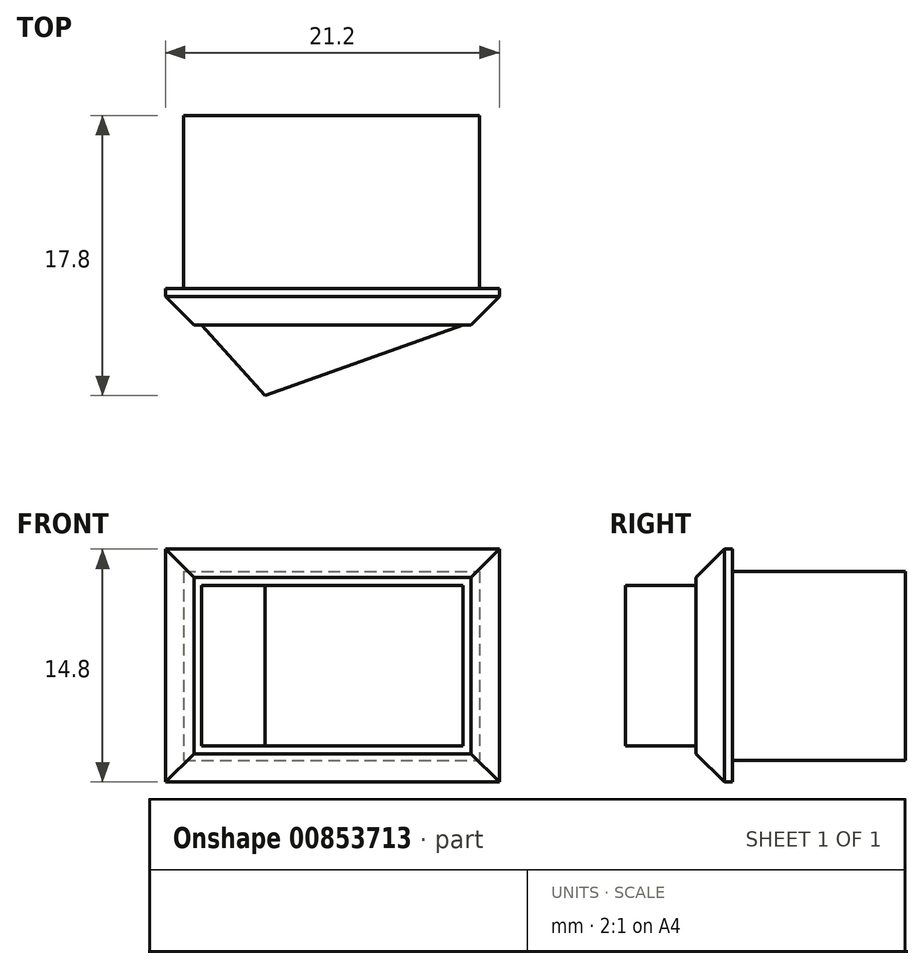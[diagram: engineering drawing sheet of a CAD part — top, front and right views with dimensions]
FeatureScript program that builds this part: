
annotation { "Feature Type Name" : "Feature", "Feature Type Description" : "" }
export const myFeature = defineFeature(function(context is Context, id is Id, definition is map)
    precondition{}
    {
        {
            var Q0;
            Q0=qCreatedBy(makeId("Front.planeOp"),FACE);
            var sketch = newSketch(context, id + "F0", { "sketchPlane" : qUnion([Q0])});
            skLineSegment(sketch, "E0.bottom", {"start": v(0, 0) * mm, "end": v(18.8, 0) * mm});
            skLineSegment(sketch, "E0.top", {"start": v(0, -12) * mm, "end": v(18.8, -12) * mm});
            skLineSegment(sketch, "E0.left", {"start": v(0, 0) * mm, "end": v(0, -12) * mm});
            skLineSegment(sketch, "E0.right", {"start": v(18.8, 0) * mm, "end": v(18.8, -12) * mm});
            skSolve(sketch);
        }
        {
            var Q0;
            Q0 = qSketchRegion(id + "F0", true);
            extrude(context, id + "F1", {"entities" : qUnion([Q0]), "depth" : 11 * mm, "offsetDistance" : 25 * mm});
        }
        {
            var Q0;
            Q0=makeQuery(id+"F1.opExtrude","CAP_FACE",FACE,{"disambiguationData":[OSD([sQuery(id+"F0.wireOp",EDGE,"E0.bottom"),sQuery(id+"F0.wireOp",EDGE,"E0.top"),sQuery(id+"F0.wireOp",EDGE,"E0.left"),sQuery(id+"F0.wireOp",EDGE,"E0.right")])],"isStart":false});
            var sketch = newSketch(context, id + "F2", { "sketchPlane" : qUnion([Q0])});
            skLineSegment(sketch, "E1.bottom", {"start": v(-1.15, 1.4) * mm, "end": v(20.05, 1.4) * mm});
            skLineSegment(sketch, "E1.top", {"start": v(-1.15, -13.4) * mm, "end": v(20.05, -13.4) * mm});
            skLineSegment(sketch, "E1.left", {"start": v(-1.15, 1.4) * mm, "end": v(-1.15, -13.4) * mm});
            skLineSegment(sketch, "E1.right", {"start": v(20.05, 1.4) * mm, "end": v(20.05, -13.4) * mm});
            skSolve(sketch);
        }
        {
            var Q0;
            Q0 = qSketchRegion(id + "F2", true);
            extrude(context, id + "F3", {"entities" : qUnion([Q0]), "operationType" : NewBodyOperationType.ADD, "depth" : 2.3 * mm, "offsetDistance" : 25 * mm});
        }
        {
            var Q0;
            Q0=makeQuery(id+"F3.opExtrude","CAP_FACE",FACE,{"disambiguationData":[OSD([sQuery(id+"F2.wireOp",EDGE,"E1.bottom"),sQuery(id+"F2.wireOp",EDGE,"E1.top"),sQuery(id+"F2.wireOp",EDGE,"E1.left"),sQuery(id+"F2.wireOp",EDGE,"E1.right")])],"isStart":false});
            chamfer(context, id + "F4", {"entities" : qUnion([Q0]), "width" : 1.8 * mm, "tangentPropagation" : true});
        }
        {
            var Q0;
            Q0=makeQuery(id+"F3.opExtrude","CAP_FACE",FACE,{"disambiguationData":[OSD([sQuery(id+"F2.wireOp",EDGE,"E1.bottom"),sQuery(id+"F2.wireOp",EDGE,"E1.top"),sQuery(id+"F2.wireOp",EDGE,"E1.left"),sQuery(id+"F2.wireOp",EDGE,"E1.right")])],"isStart":false});
            var sketch = newSketch(context, id + "F5", { "sketchPlane" : qUnion([Q0])});
            skLineSegment(sketch, "E2.0.0", {"start": v(0.65, -0.4) * mm, "end": v(0.65, -11.6) * mm});
            skLineSegment(sketch, "E2.0.1", {"start": v(0.65, -11.6) * mm, "end": v(18.25, -11.6) * mm});
            skLineSegment(sketch, "E2.0.2", {"start": v(18.25, -11.6) * mm, "end": v(18.25, -0.4) * mm});
            skLineSegment(sketch, "E2.0.3", {"start": v(18.25, -0.4) * mm, "end": v(0.65, -0.4) * mm});
            skLineSegment(sketch, "E3.0", {"start": v(1.15, -0.9) * mm, "end": v(1.15, -11.1) * mm});
            skLineSegment(sketch, "E3.1", {"start": v(17.75, -0.9) * mm, "end": v(1.15, -0.9) * mm});
            skLineSegment(sketch, "E3.2", {"start": v(17.75, -11.1) * mm, "end": v(17.75, -0.9) * mm});
            skLineSegment(sketch, "E3.3", {"start": v(1.15, -11.1) * mm, "end": v(17.75, -11.1) * mm});
            skSolve(sketch);
        }
        {
            var Q0;
            Q0=makeQuery(id+"F5.imprint","IMPRINT",FACE,{"disambiguationData":[TD([[makeQuery(id+"F5.imprint","IMPRINT",EDGE,{"derivedFrom":sQuery(id+"F5.wireOp",EDGE,"E3.0")}),1.0]])]});
            extrude(context, id + "F6", {"entities" : qUnion([Q0]), "operationType" : NewBodyOperationType.ADD, "depth" : 4.5 * mm, "offsetDistance" : 25 * mm});
        }
        {
            var Q0;
            Q0=makeQuery(id+"F6.opExtrude","SWEPT_FACE",FACE,{"disambiguationData":[OSD([sQuery(id+"F5.wireOp",EDGE,"E3.3")])]});
            var sketch = newSketch(context, id + "F7", { "sketchPlane" : qUnion([Q0])});
            skLineSegment(sketch, "E4", {"start": v(1.15, 13.3) * mm, "end": v(5.16, 17.8) * mm});
            skLineSegment(sketch, "E5", {"start": v(5.16, 17.8) * mm, "end": v(17.75, 13.3) * mm});
            skLineSegment(sketch, "E6", {"start": v(17.75, 13.3) * mm, "end": v(17.75, 17.8) * mm});
            skLineSegment(sketch, "E7", {"start": v(17.75, 17.8) * mm, "end": v(1.15, 17.8) * mm});
            skLineSegment(sketch, "E8", {"start": v(1.15, 17.8) * mm, "end": v(1.15, 13.3) * mm});
            skSolve(sketch);
        }
        {
            var Q0;
            {var subQ0=sQuery(id+"F7.wireOp",EDGE,"E4");Q0=makeQuery(id+"F7.imprint","IMPRINT",FACE,{"disambiguationData":[TD([[makeQuery(id+"F7.imprint","IMPRINT",EDGE,{"derivedFrom":subQ0}),1.0]])]});}
            var Q1;
            {var subQ0=sQuery(id+"F7.wireOp",EDGE,"E5");Q1=makeQuery(id+"F7.imprint","IMPRINT",FACE,{"disambiguationData":[TD([[makeQuery(id+"F7.imprint","IMPRINT",EDGE,{"derivedFrom":subQ0}),1.0]])]});}
            extrude(context, id + "F8", {"entities" : qUnion([Q0, Q1]), "operationType" : NewBodyOperationType.REMOVE, "oppositeDirection" : true, "depth" : 25 * mm, "offsetDistance" : 25 * mm});
        }
    });
